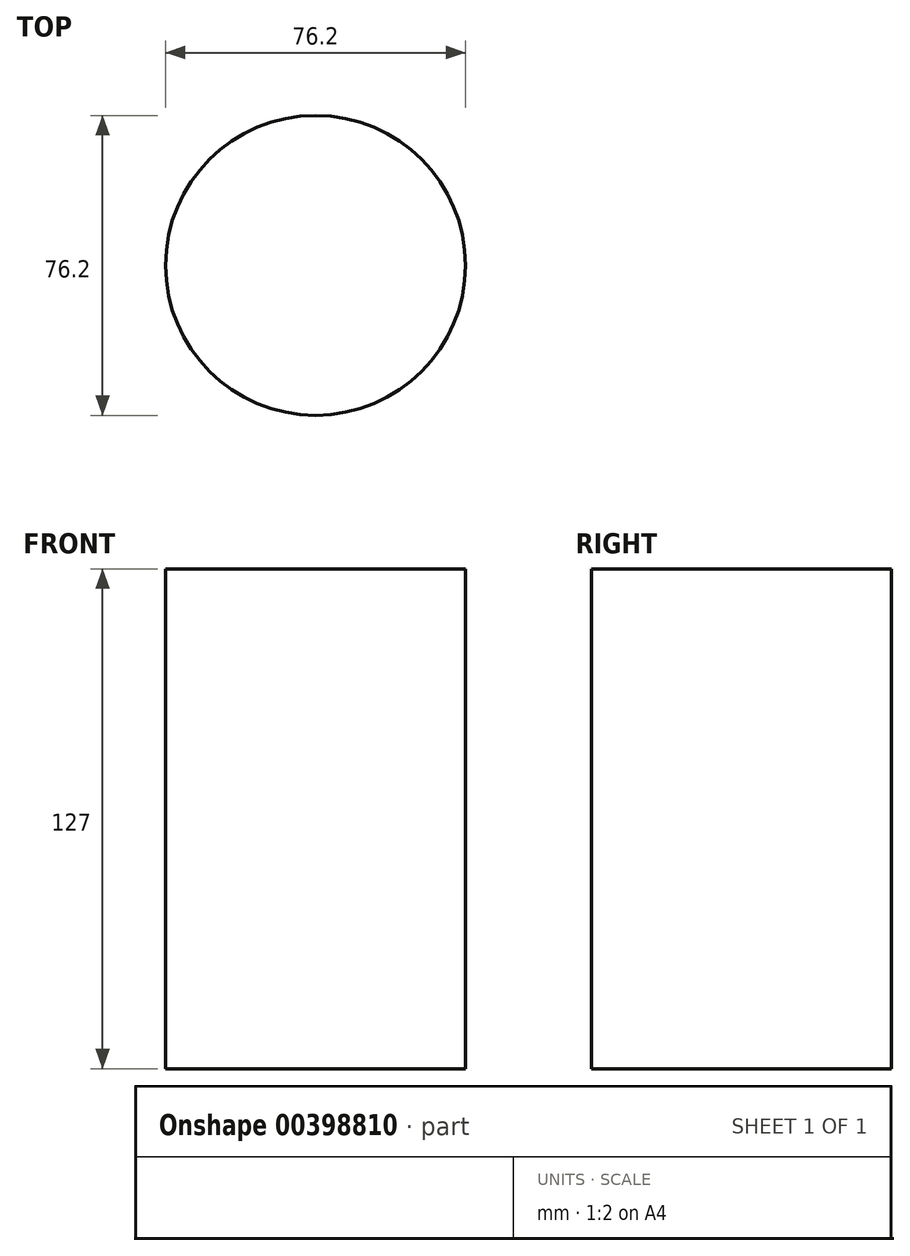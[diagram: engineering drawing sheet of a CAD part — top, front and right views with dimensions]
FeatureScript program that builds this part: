
annotation { "Feature Type Name" : "Feature", "Feature Type Description" : "" }
export const myFeature = defineFeature(function(context is Context, id is Id, definition is map)
    precondition{}
    {
        {
            var Q0;
            Q0=qCreatedBy(makeId("Top.planeOp"),FACE);
            var sketch = newSketch(context, id + "F0", { "sketchPlane" : qUnion([Q0])});
            skCircle(sketch, "E0", {"center": v(0, 0) * mm, "radius": 38.1 * mm});
            skSolve(sketch);
        }
        {
            var Q0;
            Q0 = qSketchRegion(id + "F0", true);
            extrude(context, id + "F1", {"entities" : qUnion([Q0]), "depth" : 127 * mm});
        }
    });
